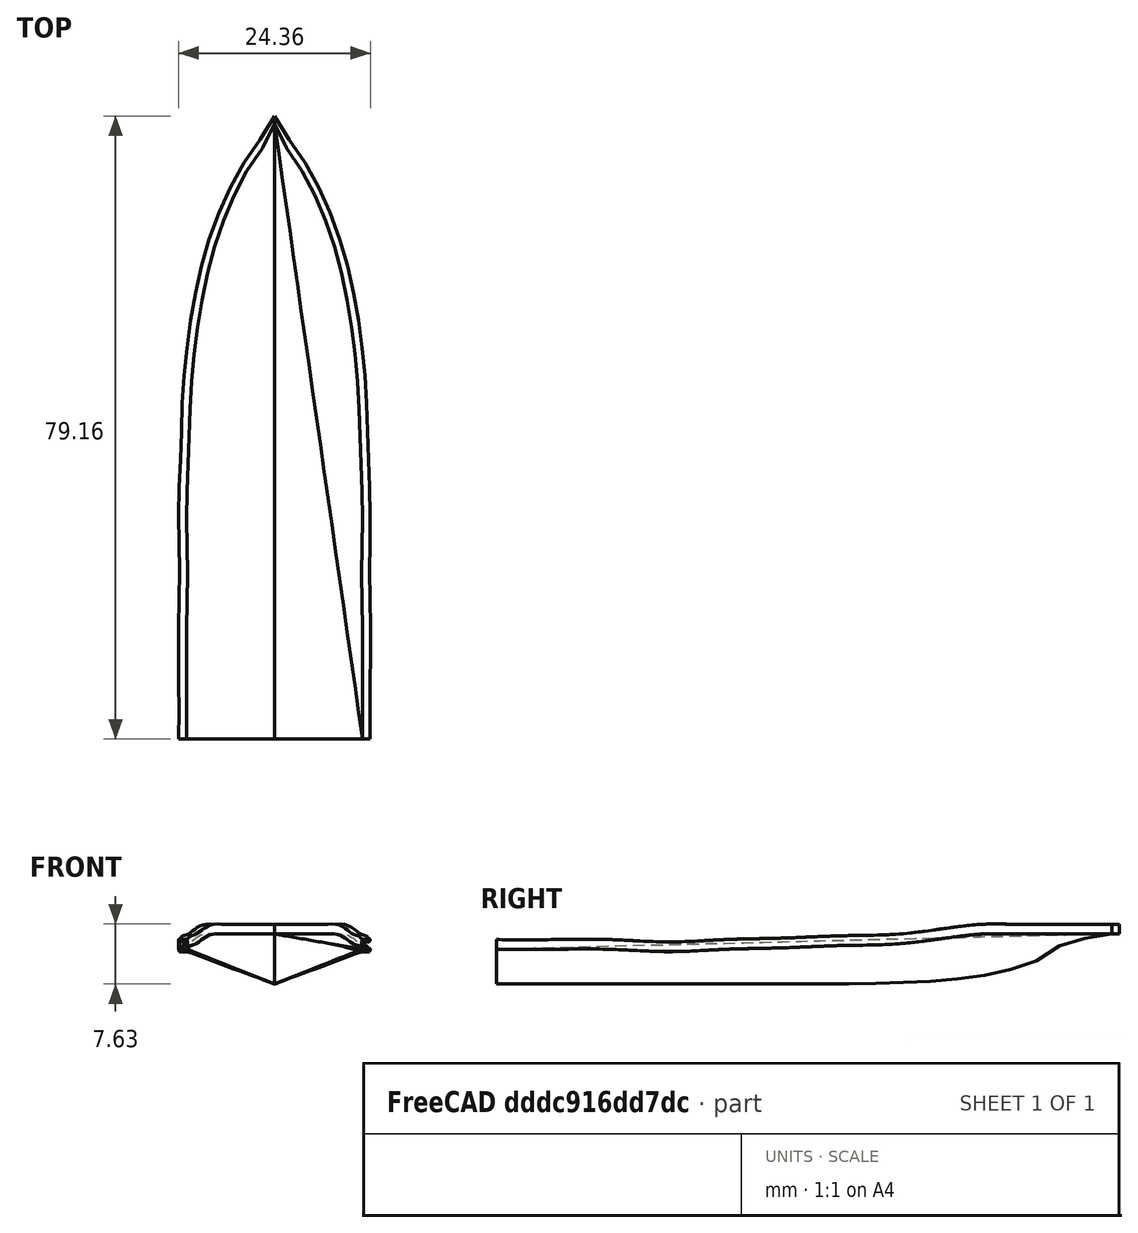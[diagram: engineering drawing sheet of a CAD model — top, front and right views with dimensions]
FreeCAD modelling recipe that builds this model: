
FCSTD DOCUMENT  (FreeCAD 0.21R33771 (Git))
Label: Ship macro
License: All rights reserved
LicenseURL: http://en.wikipedia.org/wiki/All_rights_reserved
objects: Sketcher::SketchObject×14, Part::RuledSurface×14, Part::FeaturePython×5, Part::Mirroring×4, Part::Compound×2, Part::Part2DObjectPython×1, Part::Feature×1
note: 41 computed .brp shape members not serialized (recipe doc carries the construction recipe); baked Part::Feature solids carry a one-line shape summary decoded from their .brp

FEATURE [Sketcher::SketchObject] Sketch
  FullyConstrained = false
  Placement = pos=(0,0,0) rot=(1,0,0;1.5708rad)
  sketch-geometry (6):
    g0: GeomPoint X=0 Y=6.41 Z=0
    g1: GeomPoint X=11.17 Y=6.41 Z=0
    g2: LineSegment StartX=0 StartY=2 StartZ=0 EndX=11.17 EndY=6.41 EndZ=0
    g3: LineSegment StartX=11.17 StartY=6.41 StartZ=0 EndX=12.16 EndY=6.41 EndZ=0
    g4: LineSegment StartX=12.16 StartY=6.41 StartZ=0 EndX=12.16 EndY=7.65 EndZ=0
    g5: LineSegment StartX=12.16 StartY=7.65 StartZ=0 EndX=11.17 EndY=7.65 EndZ=0
  constraints (15):
    c: PointOnObject(g2,g-2)
    c: DistanceY(g-1,g2) = 2
    c: PointOnObject(g0,g-2)
    c: DistanceY(g2,g0) = 4.41
    c: DistanceX(g0,g1) = 11.17
    c: Horizontal(g0,g1)
    c: Horizontal(g3)
    c: Coincident(g4,g3)
    c: Vertical(g4)
    c: Coincident(g5,g4)
    c: Horizontal(g5)
    c: DistanceX(g3,g3) = 0.99
    c: DistanceY(g4,g4) = 1.24
    c: DistanceX(g5,g5) = 0.99
    c: Coincident(g2,g3)
FEATURE [Sketcher::SketchObject] Sketch001
  FullyConstrained = false
  Placement = pos=(0,7.25,0) rot=(1,0,0;1.5708rad)
  sketch-geometry (6):
    g0: GeomPoint X=0 Y=6.41 Z=0
    g1: GeomPoint X=11.17 Y=6.41 Z=0
    g2: LineSegment StartX=0 StartY=2 StartZ=0 EndX=11.17 EndY=6.41 EndZ=0
    g3: LineSegment StartX=11.17 StartY=6.41 StartZ=0 EndX=12.16 EndY=6.41 EndZ=0
    g4: LineSegment StartX=12.16 StartY=6.41 StartZ=0 EndX=12.16 EndY=7.65 EndZ=0
    g5: LineSegment StartX=12.16 StartY=7.65 StartZ=0 EndX=11.17 EndY=7.65 EndZ=0
  constraints (15):
    c: PointOnObject(g2,g-2)
    c: DistanceY(g-1,g2) = 2
    c: PointOnObject(g0,g-2)
    c: DistanceY(g2,g0) = 4.41
    c: DistanceX(g0,g1) = 11.17
    c: Horizontal(g0,g1)
    c: Horizontal(g3)
    c: Coincident(g4,g3)
    c: Vertical(g4)
    c: Coincident(g5,g4)
    c: Horizontal(g5)
    c: DistanceX(g3,g3) = 0.99
    c: DistanceY(g4,g4) = 1.24
    c: DistanceX(g5,g5) = 0.99
    c: Coincident(g3,g2)
FEATURE [Sketcher::SketchObject] Sketch002
  FullyConstrained = false
  Placement = pos=(0,14.54,0) rot=(1,0,0;1.5708rad)
  sketch-geometry (6):
    g0: GeomPoint X=0 Y=6.41 Z=0
    g1: GeomPoint X=11.17 Y=6.41 Z=0
    g2: LineSegment StartX=0 StartY=2 StartZ=0 EndX=11.17 EndY=6.41 EndZ=0
    g3: LineSegment StartX=11.17 StartY=6.41 StartZ=0 EndX=12.16 EndY=6.41 EndZ=0
    g4: LineSegment StartX=12.16 StartY=6.41 StartZ=0 EndX=12.16 EndY=7.65 EndZ=0
    g5: LineSegment StartX=12.16 StartY=7.65 StartZ=0 EndX=11.17 EndY=7.65 EndZ=0
  constraints (15):
    c: PointOnObject(g2,g-2)
    c: DistanceY(g-1,g2) = 2
    c: PointOnObject(g0,g-2)
    c: DistanceY(g2,g0) = 4.41
    c: DistanceX(g0,g1) = 11.17
    c: Horizontal(g0,g1)
    c: Horizontal(g3)
    c: Coincident(g4,g3)
    c: Vertical(g4)
    c: Coincident(g5,g4)
    c: Horizontal(g5)
    c: DistanceX(g3,g3) = 0.99
    c: DistanceY(g4,g4) = 1.24
    c: DistanceX(g5,g5) = 0.99
    c: Coincident(g2,g3)
FEATURE [Sketcher::SketchObject] Sketch003
  FullyConstrained = false
  Placement = pos=(0,21.77,0) rot=(1,0,0;1.5708rad)
  sketch-geometry (6):
    g0: GeomPoint X=0 Y=6.41 Z=0
    g1: GeomPoint X=11.17 Y=6.41 Z=0
    g2: LineSegment StartX=0 StartY=2 StartZ=0 EndX=11.0686 EndY=6.1133 EndZ=0
    g3: LineSegment StartX=11.0686 StartY=6.1133 StartZ=0 EndX=12.0586 EndY=6.1133 EndZ=0
    g4: LineSegment StartX=12.0586 StartY=6.1133 StartZ=0 EndX=12.0586 EndY=7.3533 EndZ=0
    g5: LineSegment StartX=12.0586 StartY=7.3533 StartZ=0 EndX=11.0686 EndY=7.3533 EndZ=0
  constraints (15):
    c: PointOnObject(g2,g-2)
    c: DistanceY(g-1,g2) = 2
    c: PointOnObject(g0,g-2)
    c: DistanceY(g2,g0) = 4.41
    c: DistanceX(g0,g1) = 11.17
    c: Horizontal(g0,g1)
    c: Horizontal(g3)
    c: Coincident(g4,g3)
    c: Vertical(g4)
    c: Coincident(g5,g4)
    c: Horizontal(g5)
    c: DistanceX(g3,g3) = 0.99
    c: DistanceY(g4,g4) = 1.24
    c: DistanceX(g5,g5) = 0.99
    c: Coincident(g2,g3)
FEATURE [Sketcher::SketchObject] Sketch004
  FullyConstrained = false
  Placement = pos=(0,29,0) rot=(1,0,0;1.5708rad)
  sketch-geometry (6):
    g0: GeomPoint X=0 Y=6.41 Z=0
    g1: GeomPoint X=11.17 Y=6.41 Z=0
    g2: LineSegment StartX=0 StartY=2 StartZ=0 EndX=11.17 EndY=6.41 EndZ=0
    g3: LineSegment StartX=11.17 StartY=6.41 StartZ=0 EndX=12.16 EndY=6.41 EndZ=0
    g4: LineSegment StartX=12.16 StartY=6.41 StartZ=0 EndX=12.16 EndY=7.65 EndZ=0
    g5: LineSegment StartX=12.16 StartY=7.65 StartZ=0 EndX=11.17 EndY=7.65 EndZ=0
  constraints (15):
    c: PointOnObject(g2,g-2)
    c: DistanceY(g-1,g2) = 2
    c: PointOnObject(g0,g-2)
    c: DistanceY(g2,g0) = 4.41
    c: DistanceX(g0,g1) = 11.17
    c: Horizontal(g0,g1)
    c: Horizontal(g3)
    c: Coincident(g4,g3)
    c: Vertical(g4)
    c: Coincident(g5,g4)
    c: Horizontal(g5)
    c: DistanceX(g3,g3) = 0.99
    c: DistanceY(g4,g4) = 1.24
    c: DistanceX(g5,g5) = 0.99
    c: Coincident(g2,g3)
FEATURE [Sketcher::SketchObject] Sketch005
  FullyConstrained = false
  Placement = pos=(0,36.37,0) rot=(1,0,0;1.5708rad)
  sketch-geometry (6):
    g0: GeomPoint X=0 Y=6.6 Z=0
    g1: GeomPoint X=11.02 Y=6.6 Z=0
    g2: LineSegment StartX=0 StartY=2 StartZ=0 EndX=10.9331 EndY=6.6 EndZ=0
    g3: LineSegment StartX=10.9331 StartY=6.6 StartZ=0 EndX=11.9231 EndY=6.6 EndZ=0
    g4: LineSegment StartX=11.9231 StartY=6.6 StartZ=0 EndX=11.9231 EndY=7.84 EndZ=0
    g5: LineSegment StartX=11.9231 StartY=7.84 StartZ=0 EndX=10.9331 EndY=7.84 EndZ=0
  constraints (15):
    c: PointOnObject(g2,g-2)
    c: DistanceY(g-1,g2) = 2
    c: PointOnObject(g0,g-2)
    c: DistanceY(g2,g0) = 4.6
    c: DistanceX(g0,g1) = 11.02
    c: Horizontal(g0,g1)
    c: Horizontal(g3)
    c: Coincident(g4,g3)
    c: Vertical(g4)
    c: Coincident(g5,g4)
    c: Horizontal(g5)
    c: DistanceX(g3,g3) = 0.99
    c: DistanceY(g4,g4) = 1.24
    c: DistanceX(g5,g5) = 0.99
    c: Coincident(g2,g3)
FEATURE [Sketcher::SketchObject] Sketch006
  FullyConstrained = false
  Placement = pos=(0,43.66,0) rot=(1,0,0;1.5708rad)
  sketch-geometry (6):
    g0: GeomPoint X=0 Y=6.89 Z=0
    g1: GeomPoint X=10.67 Y=6.89 Z=0
    g2: LineSegment StartX=0 StartY=2.03 StartZ=0 EndX=10.67 EndY=6.89 EndZ=0
    g3: LineSegment StartX=10.67 StartY=6.89 StartZ=0 EndX=11.66 EndY=6.89 EndZ=0
    g4: LineSegment StartX=11.66 StartY=6.89 StartZ=0 EndX=11.66 EndY=8.13 EndZ=0
    g5: LineSegment StartX=11.66 StartY=8.13 StartZ=0 EndX=10.67 EndY=8.13 EndZ=0
  constraints (15):
    c: PointOnObject(g2,g-2)
    c: DistanceY(g-1,g2) = 2.03
    c: PointOnObject(g0,g-2)
    c: DistanceY(g2,g0) = 4.86
    c: DistanceX(g0,g1) = 10.67
    c: Horizontal(g0,g1)
    c: Horizontal(g3)
    c: Coincident(g4,g3)
    c: Vertical(g4)
    c: Coincident(g5,g4)
    c: Horizontal(g5)
    c: DistanceX(g3,g3) = 0.99
    c: DistanceY(g4,g4) = 1.24
    c: DistanceX(g5,g5) = 0.99
    c: Coincident(g2,g3)
FEATURE [Sketcher::SketchObject] Sketch007
  FullyConstrained = false
  Placement = pos=(0,50.95,0) rot=(1,0,0;1.5708rad)
  sketch-geometry (6):
    g0: GeomPoint X=0 Y=7.1 Z=0
    g1: GeomPoint X=9.97 Y=7.1 Z=0
    g2: LineSegment StartX=0 StartY=2.16 StartZ=0 EndX=9.97 EndY=7.1 EndZ=0
    g3: LineSegment StartX=9.97 StartY=7.1 StartZ=0 EndX=10.96 EndY=7.1 EndZ=0
    g4: LineSegment StartX=10.96 StartY=7.1 StartZ=0 EndX=10.96 EndY=8.34 EndZ=0
    g5: LineSegment StartX=10.96 StartY=8.34 StartZ=0 EndX=9.97 EndY=8.34 EndZ=0
  constraints (15):
    c: PointOnObject(g2,g-2)
    c: DistanceY(g-1,g2) = 2.16
    c: PointOnObject(g0,g-2)
    c: DistanceY(g2,g0) = 4.94
    c: DistanceX(g0,g1) = 9.97
    c: Horizontal(g0,g1)
    c: Horizontal(g3)
    c: Coincident(g4,g3)
    c: Vertical(g4)
    c: Coincident(g5,g4)
    c: Horizontal(g5)
    c: DistanceX(g3,g3) = 0.99
    c: DistanceY(g4,g4) = 1.24
    c: DistanceX(g5,g5) = 0.99
    c: Coincident(g3,g2)
FEATURE [Sketcher::SketchObject] Sketch008
  FullyConstrained = false
  Placement = pos=(0,58.24,0) rot=(1,0,0;1.5708rad)
  sketch-geometry (6):
    g0: GeomPoint X=0 Y=8 Z=0
    g1: GeomPoint X=8.71 Y=8 Z=0
    g2: LineSegment StartX=0 StartY=2.61 StartZ=0 EndX=8.71 EndY=8 EndZ=0
    g3: LineSegment StartX=8.71 StartY=8 StartZ=0 EndX=9.7 EndY=8 EndZ=0
    g4: LineSegment StartX=9.7 StartY=8 StartZ=0 EndX=9.7 EndY=9.24 EndZ=0
    g5: LineSegment StartX=9.7 StartY=9.24 StartZ=0 EndX=8.71 EndY=9.24 EndZ=0
  constraints (15):
    c: PointOnObject(g2,g-2)
    c: DistanceY(g-1,g2) = 2.61
    c: PointOnObject(g0,g-2)
    c: DistanceY(g2,g0) = 5.39
    c: DistanceX(g0,g1) = 8.71
    c: Horizontal(g0,g1)
    c: Horizontal(g3)
    c: Coincident(g4,g3)
    c: Vertical(g4)
    c: Coincident(g5,g4)
    c: Horizontal(g5)
    c: DistanceX(g3,g3) = 0.99
    c: DistanceY(g4,g4) = 1.24
    c: DistanceX(g5,g5) = 0.99
    c: Coincident(g2,g3)
FEATURE [Sketcher::SketchObject] Sketch009
  FullyConstrained = false
  Placement = pos=(0,61.89,0) rot=(1,0,0;1.5708rad)
  sketch-geometry (6):
    g0: GeomPoint X=0 Y=8.36 Z=0
    g1: GeomPoint X=7.79 Y=8.36 Z=0
    g2: LineSegment StartX=0 StartY=3.07 StartZ=0 EndX=7.79 EndY=8.35947 EndZ=0
    g3: LineSegment StartX=7.79 StartY=8.35947 StartZ=0 EndX=8.78 EndY=8.35947 EndZ=0
    g4: LineSegment StartX=8.78 StartY=8.35947 StartZ=0 EndX=8.78 EndY=9.59947 EndZ=0
    g5: LineSegment StartX=8.78 StartY=9.59947 StartZ=0 EndX=7.79 EndY=9.59947 EndZ=0
  constraints (15):
    c: PointOnObject(g2,g-2)
    c: DistanceY(g-1,g2) = 3.07
    c: PointOnObject(g0,g-2)
    c: DistanceY(g2,g0) = 5.29
    c: Horizontal(g0,g1)
    c: Horizontal(g3)
    c: Coincident(g4,g3)
    c: Vertical(g4)
    c: Coincident(g5,g4)
    c: Horizontal(g5)
    c: DistanceX(g3,g3) = 0.99
    c: DistanceY(g4,g4) = 1.24
    c: DistanceX(g5,g5) = 0.99
    c: Coincident(g3,g2)
    c: DistanceX(g0,g2) = 7.79
FEATURE [Sketcher::SketchObject] Sketch010
  FullyConstrained = false
  Placement = pos=(0,65.54,0) rot=(1,0,0;1.5708rad)
  sketch-geometry (6):
    g0: GeomPoint X=0 Y=9.01 Z=0
    g1: GeomPoint X=7.79 Y=9.01 Z=0
    g2: LineSegment StartX=0 StartY=3.89 StartZ=0 EndX=6.6 EndY=8.35947 EndZ=0
    g3: LineSegment StartX=6.6 StartY=8.35947 StartZ=0 EndX=7.59 EndY=8.35947 EndZ=0
    g4: LineSegment StartX=7.59 StartY=8.35947 StartZ=0 EndX=7.59 EndY=9.59947 EndZ=0
    g5: LineSegment StartX=7.59 StartY=9.59947 StartZ=0 EndX=6.6 EndY=9.59947 EndZ=0
  constraints (15):
    c: PointOnObject(g2,g-2)
    c: DistanceY(g-1,g2) = 3.89
    c: PointOnObject(g0,g-2)
    c: DistanceY(g2,g0) = 5.12
    c: Horizontal(g0,g1)
    c: Horizontal(g3)
    c: Coincident(g4,g3)
    c: Vertical(g4)
    c: Coincident(g5,g4)
    c: Horizontal(g5)
    c: DistanceX(g3,g3) = 0.99
    c: DistanceY(g4,g4) = 1.24
    c: DistanceX(g5,g5) = 0.99
    c: Coincident(g3,g2)
    c: DistanceX(g0,g2) = 6.6
FEATURE [Sketcher::SketchObject] Sketch011
  FullyConstrained = false
  Placement = pos=(0,69.19,0) rot=(1,0,0;1.5708rad)
  sketch-geometry (6):
    g0: GeomPoint X=0 Y=9.65 Z=0
    g1: GeomPoint X=7.79 Y=9.65 Z=0
    g2: LineSegment StartX=0 StartY=5.27 StartZ=0 EndX=5.06 EndY=8.35947 EndZ=0
    g3: LineSegment StartX=5.06 StartY=8.35947 StartZ=0 EndX=6.05 EndY=8.35947 EndZ=0
    g4: LineSegment StartX=6.05 StartY=8.35947 StartZ=0 EndX=6.05 EndY=9.59947 EndZ=0
    g5: LineSegment StartX=6.05 StartY=9.59947 StartZ=0 EndX=5.06 EndY=9.59947 EndZ=0
  constraints (15):
    c: PointOnObject(g2,g-2)
    c: DistanceY(g-1,g2) = 5.27
    c: PointOnObject(g0,g-2)
    c: DistanceY(g2,g0) = 4.38
    c: Horizontal(g0,g1)
    c: Horizontal(g3)
    c: Coincident(g4,g3)
    c: Vertical(g4)
    c: Coincident(g5,g4)
    c: Horizontal(g5)
    c: DistanceX(g3,g3) = 0.99
    c: DistanceY(g4,g4) = 1.24
    c: DistanceX(g5,g5) = 0.99
    c: Coincident(g3,g2)
    c: DistanceX(g0,g2) = 5.06
FEATURE [Sketcher::SketchObject] Sketch012
  FullyConstrained = false
  Placement = pos=(0,72.84,0) rot=(1,0,0;1.5708rad)
  sketch-geometry (6):
    g0: GeomPoint X=0 Y=10.33 Z=0
    g1: GeomPoint X=7.79 Y=10.33 Z=0
    g2: LineSegment StartX=0 StartY=7.47 StartZ=0 EndX=3.1 EndY=8.35947 EndZ=0
    g3: LineSegment StartX=3.1 StartY=8.35947 StartZ=0 EndX=4.09 EndY=8.35947 EndZ=0
    g4: LineSegment StartX=4.09 StartY=8.35947 StartZ=0 EndX=4.09 EndY=9.59947 EndZ=0
    g5: LineSegment StartX=4.09 StartY=9.59947 StartZ=0 EndX=3.1 EndY=9.59947 EndZ=0
  constraints (15):
    c: PointOnObject(g2,g-2)
    c: DistanceY(g-1,g2) = 7.47
    c: PointOnObject(g0,g-2)
    c: DistanceY(g2,g0) = 2.86
    c: Horizontal(g0,g1)
    c: Horizontal(g3)
    c: Coincident(g4,g3)
    c: Vertical(g4)
    c: Coincident(g5,g4)
    c: Horizontal(g5)
    c: DistanceX(g3,g3) = 0.99
    c: DistanceY(g4,g4) = 1.24
    c: DistanceX(g5,g5) = 0.99
    c: Coincident(g3,g2)
    c: DistanceX(g0,g2) = 3.1
FEATURE [Sketcher::SketchObject] Sketch013
  FullyConstrained = false
  Placement = pos=(0,76.49,0) rot=(1,0,0;1.5708rad)
  sketch-geometry (6):
    g0: GeomPoint X=0 Y=8.63 Z=0
    g1: GeomPoint X=7.79 Y=8.63 Z=0
    g2: LineSegment StartX=0 StartY=8 StartZ=0 EndX=0.63 EndY=8.35947 EndZ=0
    g3: LineSegment StartX=0.63 StartY=8.35947 StartZ=0 EndX=1.62 EndY=8.35947 EndZ=0
    g4: LineSegment StartX=1.62 StartY=8.35947 StartZ=0 EndX=1.62 EndY=9.59947 EndZ=0
    g5: LineSegment StartX=1.62 StartY=9.59947 StartZ=0 EndX=0.63 EndY=9.59947 EndZ=0
  constraints (15):
    c: PointOnObject(g2,g-2)
    c: DistanceY(g-1,g2) = 8
    c: PointOnObject(g0,g-2)
    c: DistanceY(g2,g0) = 0.63
    c: Horizontal(g0,g1)
    c: Horizontal(g3)
    c: Coincident(g4,g3)
    c: Vertical(g4)
    c: Coincident(g5,g4)
    c: Horizontal(g5)
    c: DistanceX(g3,g3) = 0.99
    c: DistanceY(g4,g4) = 1.24
    c: DistanceX(g5,g5) = 0.99
    c: Coincident(g3,g2)
    c: DistanceX(g0,g2) = 0.63
FEATURE [Part::Part2DObjectPython] Clone2D  label="Sketch014 (2D)"  # Draft 2D object (typed FeaturePython)
  Fuse = false
  Placement = pos=(0,77.54,0) rot=(0.57735,0.57735,0.57735;2.0944rad)
  Scale = (1,1,1)
FEATURE [Part::FeaturePython] Interpolation_Curve  # WARN: FeaturePython — macro-defined, semantics opaque (R4)
  CustomTangents = false
  DetectAligned = false
  Parameters = [0,0.0216799,0.0682225,0.122002,0.171244,0.218451,0.264875,0.357043,0.449051,0.541045,0.634047,0.725283,0.816519,0.908512,1]
  Parametrization = 0
  Periodic = false
  PointList = -> [Clone2D,Sketch013,Sketch012,Sketch011,Sketch010,Sketch009,Sketch008,Sketch007,Sketch006,Sketch005,Sketch004,Sketch003,Sketch002,Sketch001,Sketch]
  Polygonal = false
  StartOffset = 0
  Tangents = (15) [(1.61894e-15,-0.957842,-0.287294),(5.75682e-16,-0.991199,-0.132378),(-1.6959e-16,-0.943785,-0.330559),(4.21653e-17,-0.867158,-0.498032),+11 more]
  Tolerance = 1e-07
  UTurns = 0
  VTurns = 0
  WireOutput = false
FEATURE [Part::FeaturePython] Interpolation_Curve001  # WARN: FeaturePython — macro-defined, semantics opaque (R4)
  CustomTangents = false
  DetectAligned = false
  Parameters = [0,0.0223176,0.0771363,0.128668,0.177944,0.225696,0.27273,0.365429,0.45656,0.547367,0.639116,0.72913,0.819145,0.909821,1]
  Parametrization = 0
  Periodic = false
  PointList = -> [Clone2D,Sketch013,Sketch012,Sketch011,Sketch010,Sketch009,Sketch008,Sketch007,Sketch006,Sketch005,Sketch004,Sketch003,Sketch002,Sketch001,Sketch]
  Polygonal = false
  StartOffset = 0
  Tangents = (15) [(0.237939,-0.97128,2.90508e-15),(0.454218,-0.89089,-0.000122092),(0.554249,-0.832351,0.000835047),(0.419069,-0.907949,-0.00313173),+11 more]
  Tolerance = 1e-07
  UTurns = 0
  VTurns = 0
  WireOutput = false
FEATURE [Part::FeaturePython] Interpolation_Curve002  # WARN: FeaturePython — macro-defined, semantics opaque (R4)
  CustomTangents = false
  DetectAligned = false
  Parameters = [0,0.038214,0.0921414,0.142836,0.19131,0.238286,0.284555,0.375747,0.465396,0.554726,0.644984,0.733535,0.822086,0.911287,1]
  Parametrization = 0
  Periodic = false
  PointList = -> [Clone2D,Sketch013,Sketch012,Sketch011,Sketch010,Sketch009,Sketch008,Sketch007,Sketch006,Sketch005,Sketch004,Sketch003,Sketch002,Sketch001,Sketch]
  Polygonal = false
  StartOffset = 0
  Tangents = (15) [(0.468522,-0.883452,1.70217e-15),(0.556993,-0.830517,-0.000176613),(0.528432,-0.848975,0.000852248),(0.426404,-0.904528,-0.00313622),+11 more]
  Tolerance = 1e-07
  UTurns = 0
  VTurns = 0
  WireOutput = false
FEATURE [Part::FeaturePython] Interpolation_Curve003  # WARN: FeaturePython — macro-defined, semantics opaque (R4)
  CustomTangents = false
  DetectAligned = false
  Parameters = [0,0.038214,0.0921414,0.142836,0.19131,0.238286,0.284555,0.375747,0.465396,0.554726,0.644984,0.733535,0.822086,0.911287,1]
  Parametrization = 0
  Periodic = false
  PointList = -> [Clone2D,Sketch013,Sketch012,Sketch011,Sketch010,Sketch009,Sketch008,Sketch007,Sketch006,Sketch005,Sketch004,Sketch003,Sketch002,Sketch001,Sketch]
  Polygonal = false
  StartOffset = 0
  Tangents = (15) [(0.468522,-0.883452,1.70217e-15),(0.556993,-0.830517,-0.000176613),(0.528432,-0.848975,0.000852248),(0.426404,-0.904528,-0.00313622),+11 more]
  Tolerance = 1e-07
  UTurns = 0
  VTurns = 0
  WireOutput = false
FEATURE [Part::FeaturePython] Interpolation_Curve004  # WARN: FeaturePython — macro-defined, semantics opaque (R4)
  CustomTangents = false
  DetectAligned = false
  Parameters = [0,0.0223176,0.0771363,0.128668,0.177944,0.225696,0.27273,0.365429,0.45656,0.547367,0.639116,0.72913,0.819145,0.909821,1]
  Parametrization = 0
  Periodic = false
  PointList = -> [Clone2D,Sketch013,Sketch012,Sketch011,Sketch010,Sketch009,Sketch008,Sketch007,Sketch006,Sketch005,Sketch004,Sketch003,Sketch002,Sketch001,Sketch]
  Polygonal = false
  StartOffset = 0
  Tangents = (15) [(0.237939,-0.97128,2.90508e-15),(0.454218,-0.89089,-0.000122092),(0.554249,-0.832351,0.000835047),(0.419069,-0.907949,-0.00313173),+11 more]
  Tolerance = 1e-07
  UTurns = 0
  VTurns = 0
  WireOutput = false
FEATURE [Part::RuledSurface] Ruled_Surface
  Curve1 = -> Interpolation_Curve [Edge1]
  Curve2 = -> Interpolation_Curve001 [Edge1]
  Orientation = 0
FEATURE [Part::RuledSurface] Ruled_Surface001
  Curve1 = -> Interpolation_Curve002 [Edge1]
  Curve2 = -> Ruled_Surface [Edge3]
  Orientation = 0
FEATURE [Part::RuledSurface] Ruled_Surface002
  Curve1 = -> Interpolation_Curve002 [Edge1]
  Curve2 = -> Interpolation_Curve003 [Edge1]
  Orientation = 0
FEATURE [Part::RuledSurface] Ruled_Surface003
  Curve1 = -> Ruled_Surface002 [Edge3]
  Curve2 = -> Interpolation_Curve004 [Edge1]
  Orientation = 0
FEATURE [Part::RuledSurface] Ruled_Surface004
  Curve1 = -> Ruled_Surface [Edge3]
  Curve2 = -> Ruled_Surface003 [Edge3]
  Orientation = 0
FEATURE [Part::Mirroring] Part__Mirroring  label="Ruled_Surface (Mirror #1)"
  Base = (0,0,0)
  Normal = (1,0,0)
  Source = -> Ruled_Surface
FEATURE [Part::Mirroring] Part__Mirroring001  label="Ruled_Surface001 (Mirror #2)"
  Base = (0,0,0)
  Normal = (1,0,0)
  Source = -> Ruled_Surface001
FEATURE [Part::Mirroring] Part__Mirroring002  label="Ruled_Surface003 (Mirror #3)"
  Base = (0,0,0)
  Normal = (1,0,0)
  Source = -> Ruled_Surface003
FEATURE [Part::Mirroring] Part__Mirroring003  label="Ruled_Surface004 (Mirror #4)"
  Base = (0,0,0)
  Normal = (1,0,0)
  Source = -> Ruled_Surface004
FEATURE [Part::RuledSurface] Ruled_Surface005
  Curve1 = -> Part__Mirroring001 [Edge1]
  Curve2 = -> Part__Mirroring002 [Edge1]
  Orientation = 0
FEATURE [Part::RuledSurface] Ruled_Surface006
  Curve1 = -> Part__Mirroring003 [Edge3]
  Curve2 = -> Part__Mirroring [Edge3]
  Orientation = 0
FEATURE [Part::RuledSurface] Ruled_Surface007
  Curve1 = -> Part__Mirroring [Edge2]
  Curve2 = -> Ruled_Surface [Edge2]
  Orientation = 0
FEATURE [Part::RuledSurface] Ruled_Surface008
  Curve1 = -> Part__Mirroring001 [Edge3]
  Curve2 = -> Ruled_Surface007 [Edge2]
  Orientation = 0
FEATURE [Part::RuledSurface] Ruled_Surface009
  Curve1 = -> Ruled_Surface [Edge3]
  Curve2 = -> Ruled_Surface008 [Edge2]
  Orientation = 0
FEATURE [Part::Compound] Compound
  Links = -> [Ruled_Surface005,Part__Mirroring002,Part__Mirroring001,Ruled_Surface001,Ruled_Surface006,Part__Mirroring,Part__Mirroring003,Ruled_Surface004,Ruled_Surface003,Ruled_Surface,Ruled_Surface009]
FEATURE [Part::Feature] Compound_solid  label="Compound (Solid)"
  shape: bbox 24.47 x 79.16 x 7.695 mm, 11 faces (baked)
FEATURE [Part::RuledSurface] Ruled_Surface010
  Curve1 = -> Compound [Edge28]
  Curve2 = -> Compound [Edge10]
  Orientation = 0
FEATURE [Part::RuledSurface] Ruled_Surface011
  Curve1 = -> Compound [Edge8]
  Curve2 = -> Compound [Edge2]
  Orientation = 0
FEATURE [Part::RuledSurface] Ruled_Surface012
  Curve1 = -> Ruled_Surface002 [Edge2]
  Curve2 = -> Compound [Edge14]
  Orientation = 0
FEATURE [Part::RuledSurface] Ruled_Surface013
  Curve1 = -> Compound [Edge36]
  Curve2 = -> Compound [Edge32]
  Orientation = 0
FEATURE [Part::Compound] Compound001
  Links = -> [Ruled_Surface011,Ruled_Surface012,Ruled_Surface013]
